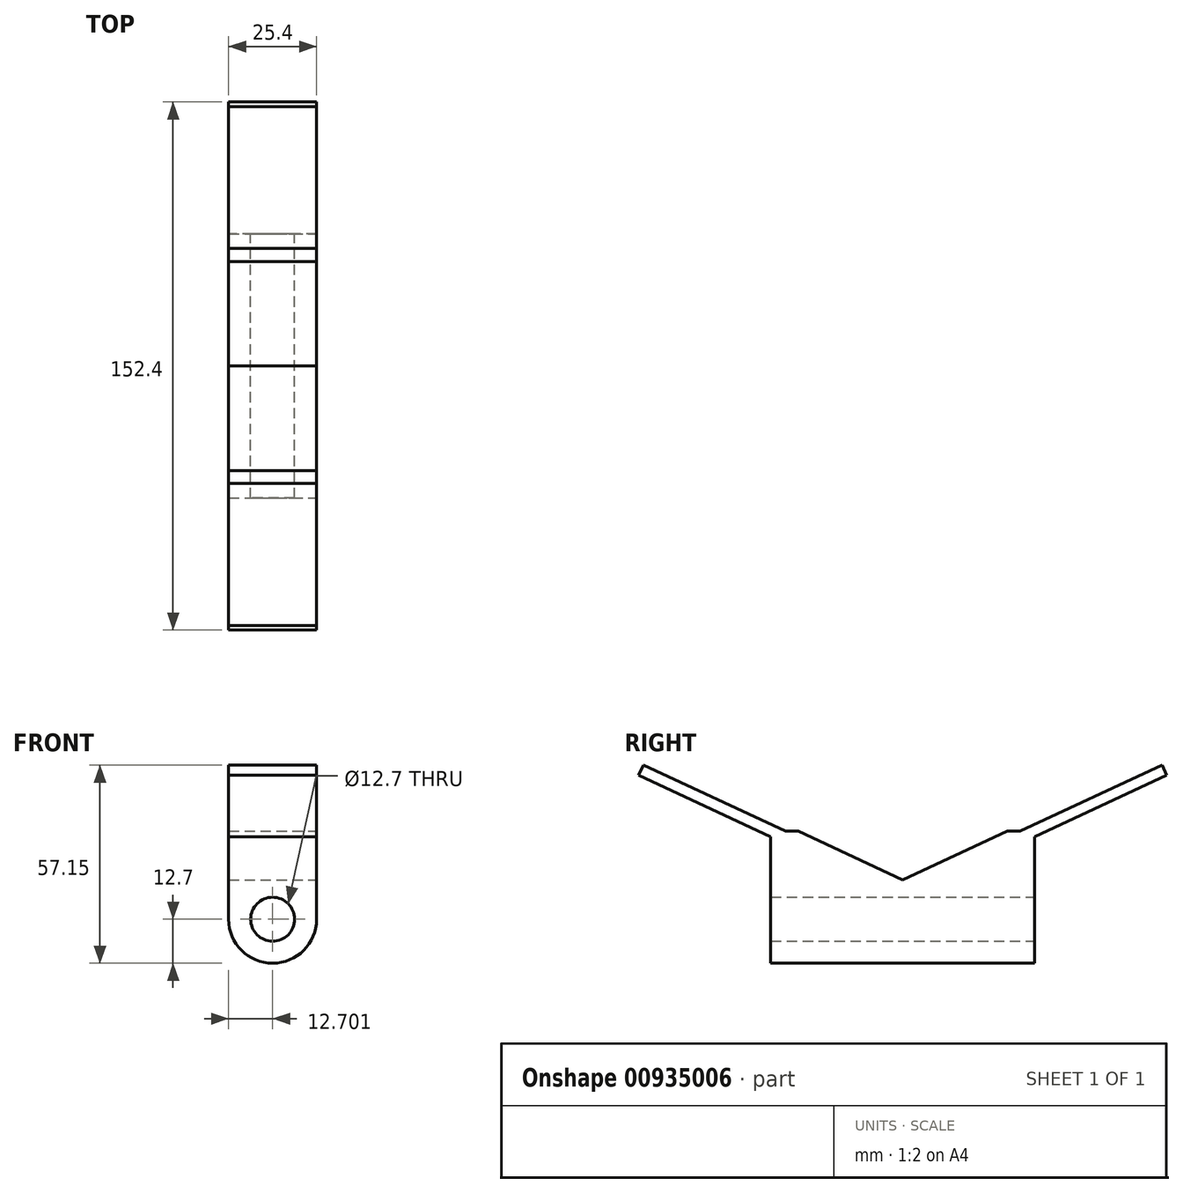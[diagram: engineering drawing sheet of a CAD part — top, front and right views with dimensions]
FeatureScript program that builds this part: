
annotation { "Feature Type Name" : "Feature", "Feature Type Description" : "" }
export const myFeature = defineFeature(function(context is Context, id is Id, definition is map)
    precondition{}
    {
        {
            var Q0;
            Q0=qCreatedBy(makeId("Front.planeOp"),FACE);
            var sketch = newSketch(context, id + "F0", { "sketchPlane" : qUnion([Q0])});
            skLineSegment(sketch, "E0.bottom", {"start": v(-2.45, 23.04) * mm, "end": v(22.95, 23.04) * mm});
            skLineSegment(sketch, "E0.top", {"start": v(10.25, -15.06) * mm, "end": v(10.25, -15.06) * mm});
            skLineSegment(sketch, "E0.left", {"start": v(-2.45, 23.04) * mm, "end": v(-2.45, -2.36) * mm});
            skLineSegment(sketch, "E0.right", {"start": v(22.95, 23.04) * mm, "end": v(22.95, -2.36) * mm});
            skPoint(sketch, "E1.visualSharp", {"position": v(-2.45, -15.06) * mm});
            skArc(sketch, "E1.filletArc", {"start": v(-2.45, -2.36) * mm, "mid": v(1.27, -11.34) * mm, "end": v(10.25, -15.06) * mm});
            skPoint(sketch, "E2.visualSharp", {"position": v(22.95, -15.06) * mm});
            skArc(sketch, "E2.filletArc", {"start": v(10.25, -15.06) * mm, "mid": v(19.23, -11.34) * mm, "end": v(22.95, -2.36) * mm});
            skCircle(sketch, "E3", {"center": v(10.25, -2.36) * mm, "radius": 6.35 * mm});
            skSolve(sketch);
        }
        {
            var Q0;
            Q0 = qSketchRegion(id + "F0", true);
            extrude(context, id + "F1", {"entities" : qUnion([Q0]), "depth" : 76.2 * mm, "offsetDistance" : 25.4 * mm, "symmetric" : true});
        }
        {
            var Q0;
            Q0=qCreatedBy(makeId("Right.planeOp"),FACE);
            var sketch = newSketch(context, id + "F2", { "sketchPlane" : qUnion([Q0])});
            skLineSegment(sketch, "E4", {"start": v(28.8, 20.67) * mm, "end": v(74.86, 42.1) * mm});
            skLineSegment(sketch, "E5.0", {"start": v(30.14, 17.79) * mm, "end": v(76.2, 39.21) * mm});
            skLineSegment(sketch, "E6", {"start": v(74.86, 42.1) * mm, "end": v(76.2, 39.21) * mm});
            skLineSegment(sketch, "E7", {"start": v(28.8, 20.67) * mm, "end": v(30.14, 17.79) * mm});
            skLineSegment(sketch, "E8.MirrorCS", {"start": v(-74.86, 42.1) * mm, "end": v(-76.2, 39.21) * mm});
            skLineSegment(sketch, "E9.MirrorCS", {"start": v(-28.8, 20.67) * mm, "end": v(-30.14, 17.79) * mm});
            skLineSegment(sketch, "E10.MirrorCS", {"start": v(-30.14, 17.79) * mm, "end": v(-76.2, 39.21) * mm});
            skLineSegment(sketch, "E11.MirrorCS", {"start": v(-28.8, 20.67) * mm, "end": v(-74.86, 42.1) * mm});
            skSolve(sketch);
        }
        {
            var Q0;
            Q0 = qSketchRegion(id + "F2", true);
            var Q1;
            Q1=makeQuery(id+"F1.opExtrude","SWEPT_FACE",FACE,{"disambiguationData":[OSD([sQuery(id+"F0.wireOp",EDGE,"E0.right")])]});
            var Q2;
            Q2=makeQuery(id+"F1.opExtrude","SWEPT_FACE",FACE,{"disambiguationData":[OSD([sQuery(id+"F0.wireOp",EDGE,"E0.left")])]});
            extrude(context, id + "F3", {"entities" : qUnion([Q0]), "operationType" : NewBodyOperationType.ADD, "endBound" : BoundingType.UP_TO_SURFACE, "depth" : 22.86 * mm, "endBoundEntityFace" : qUnion([Q1]), "offsetDistance" : 25.4 * mm, "hasSecondDirection" : true, "secondDirectionBound" : BoundingType.UP_TO_SURFACE, "secondDirectionOppositeDirection" : true, "secondDirectionDepth" : 25.4 * mm, "secondDirectionBoundEntityFace" : qUnion([Q2])});
        }
        {
            var Q0;
            Q0=qCreatedBy(makeId("Right.planeOp"),FACE);
            var sketch = newSketch(context, id + "F4", { "sketchPlane" : qUnion([Q0])});
            skLineSegment(sketch, "E12", {"start": v(37.8, 26.59) * mm, "end": v(0, 9.01) * mm});
            skLineSegment(sketch, "E13", {"start": v(0, 9.01) * mm, "end": v(-37.58, 26.49) * mm});
            skLineSegment(sketch, "E14", {"start": v(-37.58, 26.49) * mm, "end": v(37.8, 26.59) * mm});
            skSolve(sketch);
        }
        {
            var Q0;
            Q0 = qSketchRegion(id + "F4", true);
            extrude(context, id + "F5", {"entities" : qUnion([Q0]), "operationType" : NewBodyOperationType.REMOVE, "oppositeDirection" : true, "depth" : 254 * mm, "offsetDistance" : 25.4 * mm, "symmetric" : true});
        }
    });
